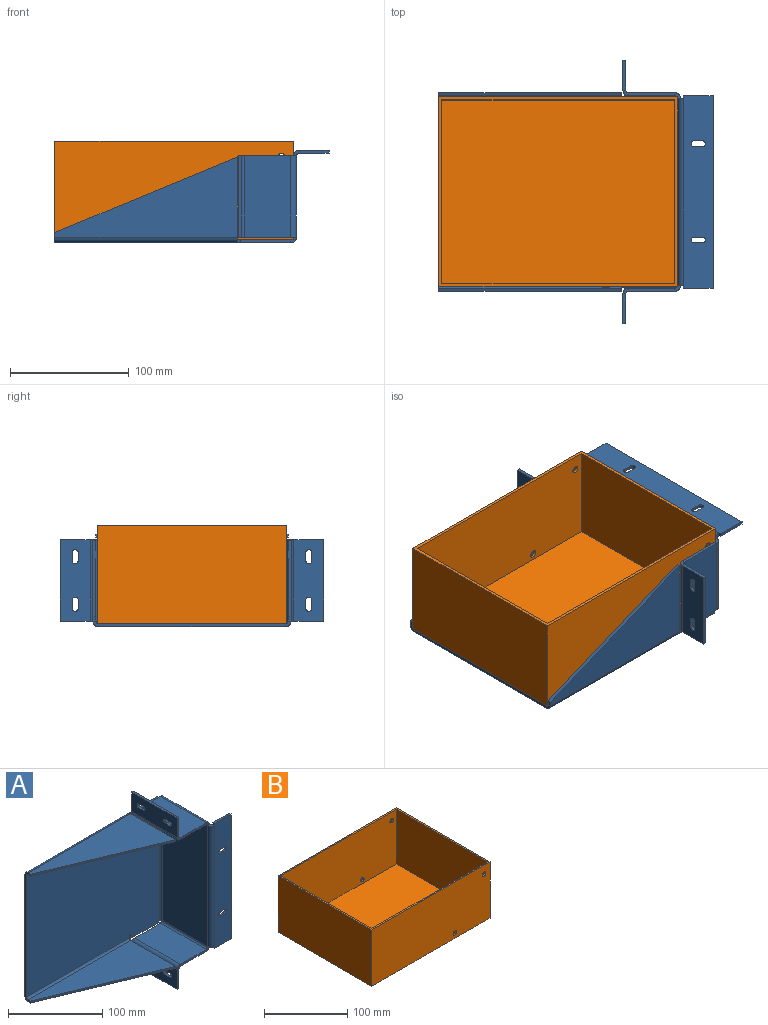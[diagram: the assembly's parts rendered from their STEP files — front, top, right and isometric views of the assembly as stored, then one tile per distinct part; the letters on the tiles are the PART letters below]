
ASSEMBLY  parts=2 mates=1
PART A: 106 faces, bbox 231x78x222 mm
  f0: plane 157.4x68.4mm, normal (1,0,0), area 10766.2mm2, adj f35,f55,f79,f104
  f1: plane 157.4x68.4mm, normal (-1,0,0), area 10766.2mm2, adj f36,f54,f80,f105
  f2: plane 2.5x2.3mm, normal (1,0,0), area 5.7mm2, adj f4,f5,f7,f33
  f3: plane 42.34x2.5mm, normal (0,0,-1), area 105.9mm2, adj f4,f5,f8,f14
  f4: plane 198.7x162mm, normal (0,1,0), area 31452.4mm2, adj f2,f3,f6,f7,f8,f9,f10,f11
  f5: plane 198.7x162mm, normal (0,-1,0), area 31452.4mm2, adj f2,f3,f6,f7,f8,f9,f10,f11
  f6: plane 157.4x2.5mm, normal (-1,0,0), area 393.5mm2, adj f4,f5,f20,f30
  f7: plane 42.34x2.5mm, normal (0,0,1), area 105.9mm2, adj f2,f4,f5,f11
  f8: plane 2.5x2.3mm, normal (1,0,0), area 5.7mm2, adj f3,f4,f5,f34
  f9: cylinder r=1.33mm len=2.66mm, axis (0,-1,0), area 10.4mm2, adj f4,f5,f10,f11
  f10: plane 2.5x2.3mm, normal (1,0,0), area 5.7mm2, adj f4,f5,f9,f29
  f11: plane 4.6x2.5mm, normal (-1,0,0), area 11.5mm2, adj f4,f5,f7,f9
  f12: plane 2.5x2.3mm, normal (1,0,0), area 5.7mm2, adj f4,f5,f13,f21
  f13: cylinder r=1.33mm len=2.66mm, axis (0,-1,0), area 10.4mm2, adj f4,f5,f12,f14
  f14: plane 4.6x2.5mm, normal (-1,0,0), area 11.5mm2, adj f3,f4,f5,f13
  f15: plane 153.7x63.66mm, normal (-0.38,-0.92,0), area 415.9mm2, adj f16,f17,f18,f19
  f16: plane 3.84x2.5mm, normal (-1,0,0), area 9.6mm2, adj f15,f18,f19,f20
  f17: plane 67.5x2.5mm, normal (1,0,0), area 168.8mm2, adj f15,f18,f19,f21
  f18: plane 153.7x67.5mm, normal (0,0,-1), area 5482.6mm2, adj f15,f16,f17,f22
  f19: plane 153.7x67.5mm, normal (0,0,1), area 5482.6mm2, adj f15,f16,f17,f23
  f20: plane 4.8x4.8mm, normal (-1,0,0), area 13.9mm2, adj f6,f16,f22,f23
  f21: plane 4.8x4.8mm, normal (1,0,0), area 13.9mm2, adj f12,f17,f22,f23
  f22: cylinder r=4.8mm len=153.7mm, axis (-1,0,0), area 1158.9mm2, adj f4,f18,f20,f21
  f23: cylinder r=2.3mm len=153.7mm, axis (-1,0,0), area 555.3mm2, adj f5,f19,f20,f21
  f24: plane 153.7x63.66mm, normal (-0.38,-0.92,0), area 415.9mm2, adj f25,f26,f27,f28
  f25: plane 67.5x2.5mm, normal (1,0,0), area 168.8mm2, adj f24,f27,f28,f29
  f26: plane 3.84x2.5mm, normal (-1,0,0), area 9.6mm2, adj f24,f27,f28,f30
  f27: plane 153.7x67.5mm, normal (0,0,1), area 5482.6mm2, adj f24,f25,f26,f31
  f28: plane 153.7x67.5mm, normal (0,0,-1), area 5482.6mm2, adj f24,f25,f26,f32
  f29: plane 4.8x4.8mm, normal (1,0,0), area 13.9mm2, adj f10,f25,f31,f32
  f30: plane 4.8x4.8mm, normal (-1,0,0), area 13.9mm2, adj f6,f26,f31,f32
  f31: cylinder r=4.8mm len=153.7mm, axis (1,0,0), area 1158.9mm2, adj f4,f27,f29,f30
  f32: cylinder r=2.3mm len=153.7mm, axis (1,0,0), area 555.3mm2, adj f5,f28,f29,f30
  f33: plane 4.8x4.8mm, normal (0,0,1), area 13.9mm2, adj f2,f35,f36,f103
  f34: plane 4.8x4.8mm, normal (0,0,-1), area 13.9mm2, adj f8,f35,f36,f77
  f35: cylinder r=4.8mm len=157.4mm, axis (0,0,1), area 1186.8mm2, adj f0,f4,f33,f34
  f36: cylinder r=2.3mm len=157.4mm, axis (0,0,1), area 568.7mm2, adj f1,f5,f33,f34
  f37: plane 2.5x2.3mm, normal (-1,0,0), area 5.7mm2, adj f48,f50,f51,f53
  f38: plane 7x2.5mm, normal (0,0,-1), area 17.5mm2, adj f39,f49,f50,f51
  f39: cylinder r=2.5mm len=5mm, axis (0,1,0), area 19.6mm2, adj f38,f40,f50,f51
  f40: plane 7x2.5mm, normal (0,0,1), area 17.5mm2, adj f39,f49,f50,f51
  f41: plane 162x2.5mm, normal (1,0,0), area 405mm2, adj f42,f48,f50,f51
  f42: plane 25.2x2.5mm, normal (0,0,-1), area 63mm2, adj f41,f43,f50,f51
  f43: plane 2.5x2.3mm, normal (-1,0,0), area 5.8mm2, adj f42,f50,f51,f52
  f44: cylinder r=2.5mm len=5mm, axis (0,1,0), area 19.6mm2, adj f45,f47,f50,f51
  f45: plane 7x2.5mm, normal (0,0,1), area 17.5mm2, adj f44,f46,f50,f51
  f46: cylinder r=2.5mm len=5mm, axis (0,1,0), area 19.6mm2, adj f45,f47,f50,f51
  f47: plane 7x2.5mm, normal (0,0,-1), area 17.5mm2, adj f44,f46,f50,f51
  f48: plane 25.2x2.5mm, normal (0,0,1), area 63mm2, adj f37,f41,f50,f51
  f49: cylinder r=2.5mm len=5mm, axis (0,1,0), area 19.6mm2, adj f38,f40,f50,f51
  f50: plane 162x25.2mm, normal (0,1,0), area 3973.1mm2, adj f37,f38,f39,f40,f41,f42,f43,f44
  f51: plane 162x25.2mm, normal (0,-1,0), area 3973.1mm2, adj f37,f38,f39,f40,f41,f42,f43,f44
  f52: plane 4.8x4.8mm, normal (0,0,-1), area 13.9mm2, adj f43,f54,f55,f78
  f53: plane 4.8x4.8mm, normal (0,0,1), area 13.9mm2, adj f37,f54,f55,f102
  f54: cylinder r=4.8mm len=157.4mm, axis (0,0,-1), area 1186.8mm2, adj f1,f51,f52,f53
  f55: cylinder r=2.3mm len=157.4mm, axis (0,0,-1), area 568.7mm2, adj f0,f50,f52,f53
  f56: plane 38.9x2.5mm, normal (0,1,0), area 97.2mm2, adj f58,f59,f73,f77
  f57: plane 38.9x2.5mm, normal (0,-1,0), area 97.2mm2, adj f58,f59,f74,f78
  f58: plane 68.4x38.9mm, normal (0,0,-1), area 2660.8mm2, adj f56,f57,f76,f79
  f59: plane 68.4x38.9mm, normal (0,0,1), area 2660.8mm2, adj f56,f57,f75,f80
  f60: plane 68.4x2.5mm, normal (0,0,-1), area 171mm2, adj f61,f70,f71,f72
  f61: plane 25.2x2.5mm, normal (0,1,0), area 63mm2, adj f60,f71,f72,f73
  f62: cylinder r=2.5mm len=5mm, axis (1,0,0), area 19.6mm2, adj f63,f69,f71,f72
  f63: plane 7x2.5mm, normal (0,0,-1), area 17.5mm2, adj f62,f64,f71,f72
  f64: cylinder r=2.5mm len=5mm, axis (1,0,0), area 19.6mm2, adj f63,f69,f71,f72
  f65: plane 7x2.5mm, normal (0,0,1), area 17.5mm2, adj f66,f68,f71,f72
  f66: cylinder r=2.5mm len=5mm, axis (1,0,0), area 19.6mm2, adj f65,f67,f71,f72
  f67: plane 7x2.5mm, normal (0,0,-1), area 17.5mm2, adj f66,f68,f71,f72
  f68: cylinder r=2.5mm len=5mm, axis (1,0,0), area 19.6mm2, adj f65,f67,f71,f72
  f69: plane 7x2.5mm, normal (0,0,1), area 17.5mm2, adj f62,f64,f71,f72
  f70: plane 25.2x2.5mm, normal (0,-1,0), area 63mm2, adj f60,f71,f72,f74
  f71: plane 68.4x25.2mm, normal (1,0,0), area 1614.4mm2, adj f60,f61,f62,f63,f64,f65,f66,f67
  f72: plane 68.4x25.2mm, normal (-1,0,0), area 1614.4mm2, adj f60,f61,f62,f63,f64,f65,f66,f67
  f73: plane 4.8x4.8mm, normal (0,1,0), area 13.9mm2, adj f56,f61,f75,f76
  f74: plane 4.8x4.8mm, normal (0,-1,0), area 13.9mm2, adj f57,f70,f75,f76
  f75: cylinder r=4.8mm len=68.4mm, axis (0,1,0), area 515.7mm2, adj f59,f72,f73,f74
  f76: cylinder r=2.3mm len=68.4mm, axis (0,1,0), area 247.1mm2, adj f58,f71,f73,f74
  f77: plane 4.8x4.8mm, normal (0,1,0), area 13.9mm2, adj f34,f56,f79,f80
  f78: plane 4.8x4.8mm, normal (0,-1,0), area 13.9mm2, adj f52,f57,f79,f80
  f79: cylinder r=4.8mm len=68.4mm, axis (0,1,0), area 515.7mm2, adj f0,f58,f77,f78
  f80: cylinder r=2.3mm len=68.4mm, axis (0,1,0), area 247.1mm2, adj f1,f59,f77,f78
  f81: plane 38.9x2.5mm, normal (0,-1,0), area 97.3mm2, adj f83,f84,f98,f102
  f82: plane 38.9x2.5mm, normal (0,1,0), area 97.3mm2, adj f83,f84,f99,f103
  f83: plane 68.4x38.9mm, normal (0,0,1), area 2660.8mm2, adj f81,f82,f101,f104
  f84: plane 68.4x38.9mm, normal (0,0,-1), area 2660.8mm2, adj f81,f82,f100,f105
  f85: plane 68.4x2.5mm, normal (0,0,1), area 171mm2, adj f86,f95,f96,f97
  f86: plane 25.2x2.5mm, normal (0,-1,0), area 63mm2, adj f85,f96,f97,f98
  f87: cylinder r=2.5mm len=5mm, axis (1,0,0), area 19.6mm2, adj f88,f94,f96,f97
  f88: plane 7x2.5mm, normal (0,0,1), area 17.5mm2, adj f87,f89,f96,f97
  f89: cylinder r=2.5mm len=5mm, axis (1,0,0), area 19.6mm2, adj f88,f94,f96,f97
  f90: plane 7x2.5mm, normal (0,0,-1), area 17.5mm2, adj f91,f93,f96,f97
  f91: cylinder r=2.5mm len=5mm, axis (1,0,0), area 19.6mm2, adj f90,f92,f96,f97
  f92: plane 7x2.5mm, normal (0,0,1), area 17.5mm2, adj f91,f93,f96,f97
  f93: cylinder r=2.5mm len=5mm, axis (1,0,0), area 19.6mm2, adj f90,f92,f96,f97
  f94: plane 7x2.5mm, normal (0,0,-1), area 17.5mm2, adj f87,f89,f96,f97
  f95: plane 25.2x2.5mm, normal (0,1,0), area 63mm2, adj f85,f96,f97,f99
  f96: plane 68.4x25.2mm, normal (1,0,0), area 1614.4mm2, adj f85,f86,f87,f88,f89,f90,f91,f92
  f97: plane 68.4x25.2mm, normal (-1,0,0), area 1614.4mm2, adj f85,f86,f87,f88,f89,f90,f91,f92
  f98: plane 4.8x4.8mm, normal (0,-1,0), area 13.9mm2, adj f81,f86,f100,f101
  f99: plane 4.8x4.8mm, normal (0,1,0), area 13.9mm2, adj f82,f95,f100,f101
  f100: cylinder r=4.8mm len=68.4mm, axis (0,-1,0), area 515.7mm2, adj f84,f97,f98,f99
  f101: cylinder r=2.3mm len=68.4mm, axis (0,-1,0), area 247.1mm2, adj f83,f96,f98,f99
  f102: plane 4.8x4.8mm, normal (0,-1,0), area 13.9mm2, adj f53,f81,f104,f105
  f103: plane 4.8x4.8mm, normal (0,1,0), area 13.9mm2, adj f33,f82,f104,f105
  f104: cylinder r=4.8mm len=68.4mm, axis (0,-1,0), area 515.7mm2, adj f0,f83,f102,f103
  f105: cylinder r=2.3mm len=68.4mm, axis (0,-1,0), area 247.1mm2, adj f1,f84,f102,f103
PART B: 15 faces, bbox 201x160x83 mm
  f0: plane 201x160mm, normal (0,0,1), area 1780mm2, adj f1,f2,f3,f4,f6,f7,f8,f9
  f1: plane 201x83mm, normal (0,1,0), area 16626.5mm2, adj f0,f2,f4,f5,f13,f14
  f2: plane 160x83mm, normal (-1,0,0), area 13280mm2, adj f0,f1,f3,f5
  f3: plane 201x83mm, normal (0,-1,0), area 16626.5mm2, adj f0,f2,f4,f5,f11,f12
  f4: plane 160x83mm, normal (1,0,0), area 13280mm2, adj f0,f1,f3,f5
  f5: plane 201x160mm, normal (0,0,-1), area 32160mm2, adj f1,f2,f3,f4
  f6: plane 196x80.5mm, normal (0,-1,0), area 15721.5mm2, adj f0,f7,f9,f10,f13,f14
  f7: plane 155x80.5mm, normal (1,0,0), area 12477.5mm2, adj f0,f6,f8,f10
  f8: plane 196x80.5mm, normal (0,1,0), area 15721.5mm2, adj f0,f7,f9,f10,f11,f12
  f9: plane 155x80.5mm, normal (-1,0,0), area 12477.5mm2, adj f0,f6,f8,f10
  f10: plane 196x155mm, normal (0,0,1), area 30380mm2, adj f6,f7,f8,f9
  f11: cylinder r=3mm len=6mm, axis (0,-1,0), area 47.1mm2, adj f3,f8
  f12: cylinder r=3mm len=6mm, axis (0,-1,0), area 47.1mm2, adj f3,f8
  f13: cylinder r=3mm len=6mm, axis (0,-1,0), area 47.1mm2, adj f1,f6
  f14: cylinder r=3mm len=6mm, axis (0,-1,0), area 47.1mm2, adj f1,f6
PLACE A rot(axis=(-1,0,0),90deg) t=(4.4,-60.59,-14.47)mm
PLACE B t=(-36.19,-20.96,-53.26)mm
MATE fastened B.f4 <-> A.f1  axis (1,0,0) through (94.66,20.41,-11.76)mm
